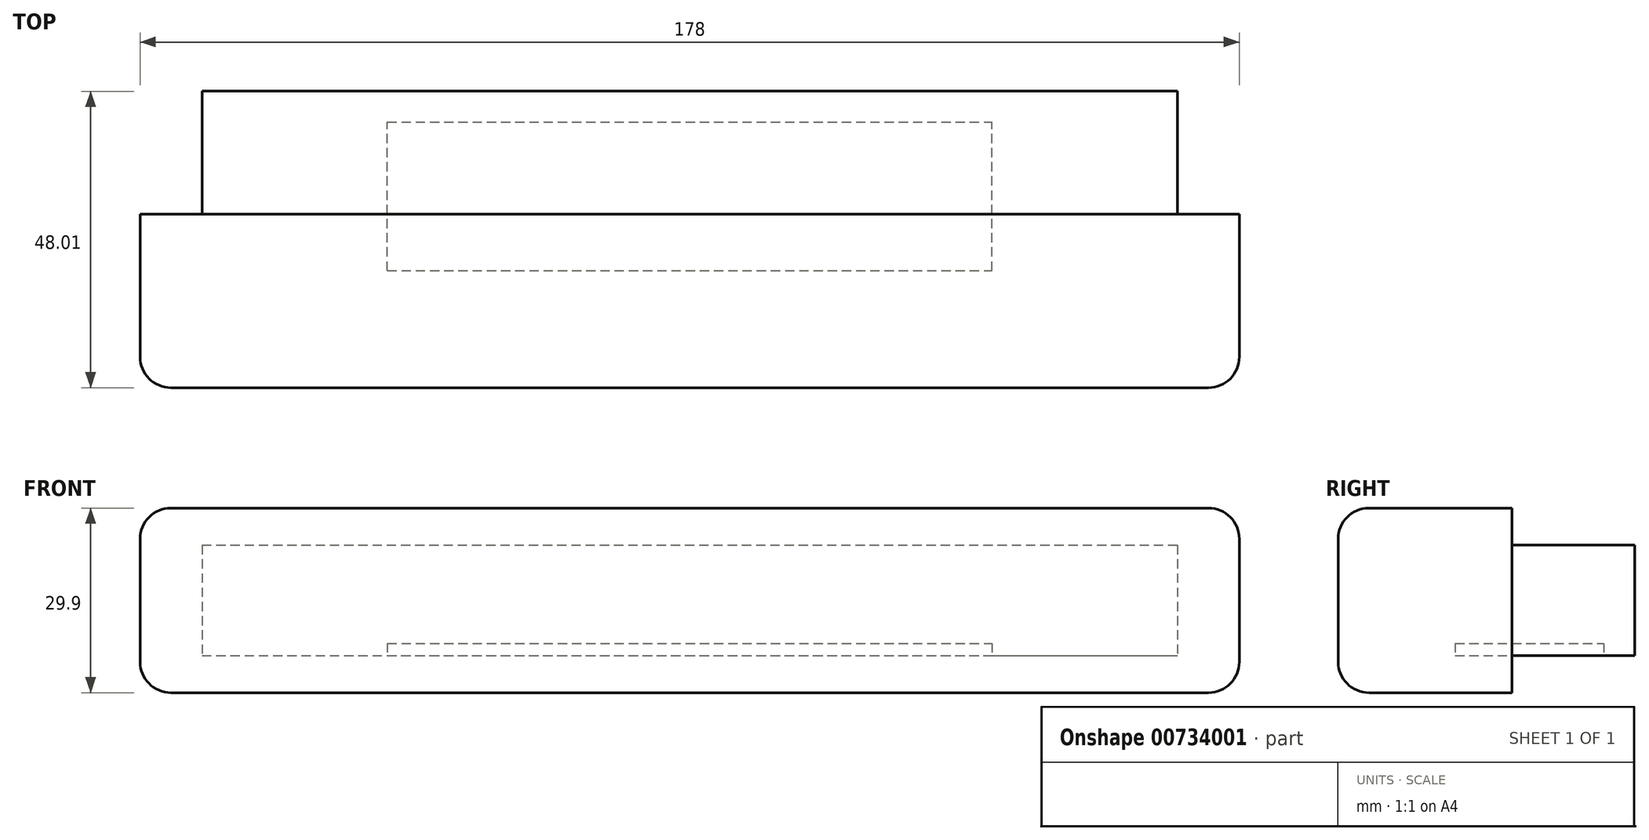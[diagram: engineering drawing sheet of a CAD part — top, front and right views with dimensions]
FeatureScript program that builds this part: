
annotation { "Feature Type Name" : "Feature", "Feature Type Description" : "" }
export const myFeature = defineFeature(function(context is Context, id is Id, definition is map)
    precondition{}
    {
        {
            var Q0;
            Q0=qCreatedBy(makeId("Top.planeOp"),FACE);
            var sketch = newSketch(context, id + "F0", { "sketchPlane" : qUnion([Q0])});
            skLineSegment(sketch, "E0.bottom", {"start": v(-193.17, 48.01) * mm, "end": v(-15.17, 48.01) * mm});
            skLineSegment(sketch, "E0.top", {"start": v(-193.17, 0) * mm, "end": v(-15.17, 0) * mm});
            skLineSegment(sketch, "E0.left", {"start": v(-193.17, 48.01) * mm, "end": v(-193.17, 0) * mm});
            skLineSegment(sketch, "E0.right", {"start": v(-15.17, 48.01) * mm, "end": v(-15.17, 0) * mm});
            skSolve(sketch);
        }
        {
            var Q0;
            Q0=makeQuery(id+"F0.imprint","IMPRINT",FACE,{"disambiguationData":[TD([[makeQuery(id+"F0.imprint","IMPRINT",EDGE,{"derivedFrom":sQuery(id+"F0.wireOp",EDGE,"E0.bottom")}),-1.0]])]});
            extrude(context, id + "F1", {"entities" : qUnion([Q0]), "depth" : 17.9 * mm, "offsetDistance" : 25 * mm});
        }
        {
            var Q0;
            Q0=makeQuery(id+"F1.opExtrude","SWEPT_FACE",FACE,{"disambiguationData":[OSD([sQuery(id+"F0.wireOp",EDGE,"E0.bottom")])]});
            var sketch = newSketch(context, id + "F2", { "sketchPlane" : qUnion([Q0])});
            skLineSegment(sketch, "E1.bottom", {"start": v(15.17, 17.9) * mm, "end": v(25.22, 17.9) * mm});
            skLineSegment(sketch, "E1.top", {"start": v(15.17, 0) * mm, "end": v(25.22, 0) * mm});
            skLineSegment(sketch, "E1.left", {"start": v(15.17, 17.9) * mm, "end": v(15.17, 0) * mm});
            skLineSegment(sketch, "E1.right", {"start": v(25.22, 17.9) * mm, "end": v(25.22, 0) * mm});
            skLineSegment(sketch, "E2.bottom", {"start": v(193.17, 17.9) * mm, "end": v(183.12, 17.9) * mm});
            skLineSegment(sketch, "E2.top", {"start": v(193.17, 0) * mm, "end": v(183.12, 0) * mm});
            skLineSegment(sketch, "E2.left", {"start": v(193.17, 17.9) * mm, "end": v(193.17, 0) * mm});
            skLineSegment(sketch, "E2.right", {"start": v(183.12, 17.9) * mm, "end": v(183.12, 0) * mm});
            skSolve(sketch);
        }
        {
            var Q0;
            Q0 = qSketchRegion(id + "F2", true);
            extrude(context, id + "F3", {"entities" : qUnion([Q0]), "operationType" : NewBodyOperationType.REMOVE, "oppositeDirection" : true, "depth" : 19.9 * mm, "offsetDistance" : 25 * mm});
        }
        {
            var Q0;
            Q0=makeQuery(id+"F1.opExtrude","CAP_FACE",FACE,{"disambiguationData":[OSD([sQuery(id+"F0.wireOp",EDGE,"E0.bottom"),sQuery(id+"F0.wireOp",EDGE,"E0.top"),sQuery(id+"F0.wireOp",EDGE,"E0.left"),sQuery(id+"F0.wireOp",EDGE,"E0.right")])],"isStart":false});
            var sketch = newSketch(context, id + "F4", { "sketchPlane" : qUnion([Q0])});
            skLineSegment(sketch, "E3.bottom", {"start": v(-15.17, 0) * mm, "end": v(-193.17, 0) * mm});
            skLineSegment(sketch, "E3.top", {"start": v(-15.17, 28.11) * mm, "end": v(-193.17, 28.11) * mm});
            skLineSegment(sketch, "E3.left", {"start": v(-15.17, 0) * mm, "end": v(-15.17, 28.11) * mm});
            skLineSegment(sketch, "E3.right", {"start": v(-193.17, 0) * mm, "end": v(-193.17, 28.11) * mm});
            skSolve(sketch);
        }
        {
            var Q0;
            Q0=makeQuery(id+"F1.opExtrude","CAP_FACE",FACE,{"disambiguationData":[OSD([sQuery(id+"F0.wireOp",EDGE,"E0.bottom"),sQuery(id+"F0.wireOp",EDGE,"E0.top"),sQuery(id+"F0.wireOp",EDGE,"E0.left"),sQuery(id+"F0.wireOp",EDGE,"E0.right")])],"isStart":true});
            var sketch = newSketch(context, id + "F5", { "sketchPlane" : qUnion([Q0])});
            skLineSegment(sketch, "E4.bottom", {"start": v(-15.17, -28.11) * mm, "end": v(-193.17, -28.11) * mm});
            skLineSegment(sketch, "E4.top", {"start": v(-15.17, 0) * mm, "end": v(-193.17, 0) * mm});
            skLineSegment(sketch, "E4.left", {"start": v(-15.17, -28.11) * mm, "end": v(-15.17, 0) * mm});
            skLineSegment(sketch, "E4.right", {"start": v(-193.17, -28.11) * mm, "end": v(-193.17, 0) * mm});
            skSolve(sketch);
        }
        {
            var Q0;
            Q0 = qSketchRegion(id + "F4", true);
            var Q1;
            Q1=makeQuery(id+"F5.imprint","IMPRINT",FACE,{"disambiguationData":[TD([[makeQuery(id+"F5.imprint","IMPRINT",EDGE,{"derivedFrom":sQuery(id+"F5.wireOp",EDGE,"E4.top")}),-1.0]])]});
            extrude(context, id + "F6", {"entities" : qUnion([Q0, Q1]), "operationType" : NewBodyOperationType.ADD, "depth" : 6 * mm, "offsetDistance" : 25 * mm, "hasSecondDirection" : true, "secondDirectionOppositeDirection" : true, "secondDirectionDepth" : 6 * mm});
        }
        {
            var Q0;
            Q0=makeQuery(id+"F1.opExtrude","CAP_FACE",FACE,{"disambiguationData":[OSD([sQuery(id+"F0.wireOp",EDGE,"E0.bottom"),sQuery(id+"F0.wireOp",EDGE,"E0.top"),sQuery(id+"F0.wireOp",EDGE,"E0.left"),sQuery(id+"F0.wireOp",EDGE,"E0.right")])],"isStart":true});
            var sketch = newSketch(context, id + "F7", { "sketchPlane" : qUnion([Q0])});
            skLineSegment(sketch, "E5.bottom", {"start": v(-153.12, -18.95) * mm, "end": v(-55.22, -18.95) * mm});
            skLineSegment(sketch, "E5.top", {"start": v(-153.12, -43.01) * mm, "end": v(-55.22, -43.01) * mm});
            skLineSegment(sketch, "E5.left", {"start": v(-153.12, -18.95) * mm, "end": v(-153.12, -43.01) * mm});
            skLineSegment(sketch, "E5.right", {"start": v(-55.22, -18.95) * mm, "end": v(-55.22, -43.01) * mm});
            skSolve(sketch);
        }
        {
            var Q0;
            Q0 = qSketchRegion(id + "F7", true);
            extrude(context, id + "F8", {"entities" : qUnion([Q0]), "operationType" : NewBodyOperationType.REMOVE, "oppositeDirection" : true, "depth" : 2 * mm, "offsetDistance" : 25 * mm});
        }
        {
            var Q0;
            Q0=makeQuery(id+"F6.opExtrude","CAP_EDGE",EDGE,{"disambiguationData":[OSD([sQuery(id+"F5.wireOp",EDGE,"E4.top")])],"isStart":true});
            var Q1;
            Q1=makeQuery(id+"F6.opExtrude","CAP_EDGE",EDGE,{"disambiguationData":[OSD([sQuery(id+"F4.wireOp",EDGE,"E3.bottom")])],"isStart":false});
            var Q2;
            Q2=makeQuery(id+"F6.boolean.opBoolean","MERGE",EDGE,{"derivedFrom":[makeQuery(id+"F1.opExtrude","SWEPT_EDGE",EDGE,{"disambiguationData":[OSD([sQuery(id+"F0.wireOp",EDGE,"E0.top"),sQuery(id+"F0.wireOp",EDGE,"E0.right")])]}),makeQuery(id+"F6.opExtrude","SWEPT_EDGE",EDGE,{"disambiguationData":[OSD([sQuery(id+"F4.wireOp",EDGE,"E3.bottom"),sQuery(id+"F4.wireOp",EDGE,"E3.left")])]}),makeQuery(id+"F6.opExtrude","SWEPT_EDGE",EDGE,{"disambiguationData":[OSD([sQuery(id+"F5.wireOp",EDGE,"E4.top"),sQuery(id+"F5.wireOp",EDGE,"E4.left")])]})]});
            var Q3;
            Q3=makeQuery(id+"F6.boolean.opBoolean","MERGE",EDGE,{"derivedFrom":[makeQuery(id+"F1.opExtrude","SWEPT_EDGE",EDGE,{"disambiguationData":[OSD([sQuery(id+"F0.wireOp",EDGE,"E0.top"),sQuery(id+"F0.wireOp",EDGE,"E0.left")])]}),makeQuery(id+"F6.opExtrude","SWEPT_EDGE",EDGE,{"disambiguationData":[OSD([sQuery(id+"F4.wireOp",EDGE,"E3.bottom"),sQuery(id+"F4.wireOp",EDGE,"E3.right")])]}),makeQuery(id+"F6.opExtrude","SWEPT_EDGE",EDGE,{"disambiguationData":[OSD([sQuery(id+"F5.wireOp",EDGE,"E4.top"),sQuery(id+"F5.wireOp",EDGE,"E4.right")])]})]});
            var Q4;
            Q4=makeQuery(id+"F6.opExtrude","CAP_EDGE",EDGE,{"disambiguationData":[OSD([sQuery(id+"F5.wireOp",EDGE,"E4.left")])],"isStart":true});
            var Q5;
            Q5=makeQuery(id+"F6.opExtrude","CAP_EDGE",EDGE,{"disambiguationData":[OSD([sQuery(id+"F4.wireOp",EDGE,"E3.left")])],"isStart":false});
            var Q6;
            Q6=makeQuery(id+"F6.opExtrude","CAP_EDGE",EDGE,{"disambiguationData":[OSD([sQuery(id+"F5.wireOp",EDGE,"E4.right")])],"isStart":true});
            var Q7;
            Q7=makeQuery(id+"F6.opExtrude","CAP_EDGE",EDGE,{"disambiguationData":[OSD([sQuery(id+"F4.wireOp",EDGE,"E3.right")])],"isStart":false});
            fillet(context, id + "F9", {"entities" : qUnion([Q0, Q1, Q2, Q3, Q4, Q5, Q6, Q7]), "radius" : 5 * mm, "tangentPropagation" : true, "allowEdgeOverflow" : false});
        }
    });
